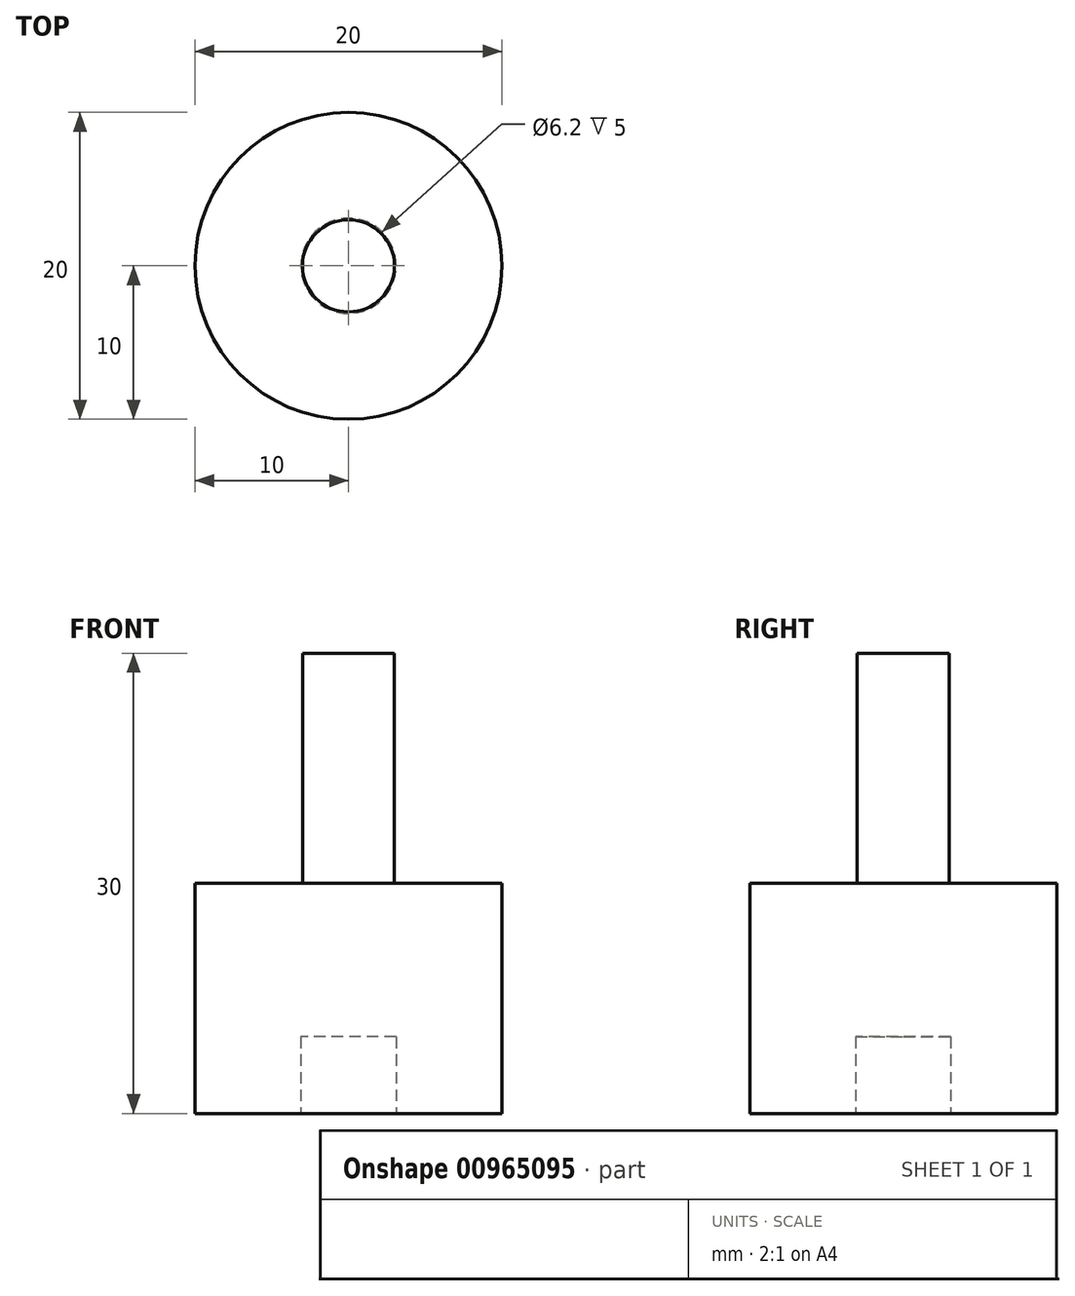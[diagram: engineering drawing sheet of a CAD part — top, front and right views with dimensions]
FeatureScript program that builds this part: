
annotation { "Feature Type Name" : "Feature", "Feature Type Description" : "" }
export const myFeature = defineFeature(function(context is Context, id is Id, definition is map)
    precondition{}
    {
        {
            var Q0;
            Q0=qCreatedBy(makeId("Top.planeOp"),FACE);
            var sketch = newSketch(context, id + "F0", { "sketchPlane" : qUnion([Q0])});
            skCircle(sketch, "E0", {"center": v(0, 0) * mm, "radius": 10 * mm});
            skCircle(sketch, "E1", {"center": v(0, 0) * mm, "radius": 3.1 * mm});
            skSolve(sketch);
        }
        {
            var Q0;
            Q0=makeQuery(id+"F0.imprint","IMPRINT",FACE,{"disambiguationData":[TD([[makeQuery(id+"F0.imprint","IMPRINT",EDGE,{"derivedFrom":sQuery(id+"F0.wireOp",EDGE,"E0")}),1.0]])]});
            extrude(context, id + "F1", {"entities" : qUnion([Q0]), "depth" : 5 * mm, "offsetDistance" : 25 * mm});
        }
        {
            var Q0;
            Q0=makeQuery(id+"F1.opExtrude","CAP_FACE",FACE,{"disambiguationData":[OSD([sQuery(id+"F0.wireOp",EDGE,"E0"),sQuery(id+"F0.wireOp",EDGE,"E1")])],"isStart":false});
            var sketch = newSketch(context, id + "F2", { "sketchPlane" : qUnion([Q0])});
            skCircle(sketch, "E2", {"center": v(0, 0) * mm, "radius": 3 * mm});
            skSolve(sketch);
        }
        {
            var Q0;
            Q0=makeQuery(id+"F2.imprint","IMPRINT",FACE,{"disambiguationData":[TD([[makeQuery(id+"F2.imprint","IMPRINT",EDGE,{"derivedFrom":makeQuery(id+"F1.opExtrude","CAP_EDGE",EDGE,{"disambiguationData":[OSD([sQuery(id+"F0.wireOp",EDGE,"E0")])],"isStart":false})}),1.0]])]});
            var Q1;
            Q1=makeQuery(id+"F2.imprint","IMPRINT",FACE,{"disambiguationData":[TD([[makeQuery(id+"F2.imprint","IMPRINT",EDGE,{"derivedFrom":sQuery(id+"F2.wireOp",EDGE,"E2")}),-1.0]])]});
            extrude(context, id + "F3", {"entities" : qUnion([Q0, Q1]), "operationType" : NewBodyOperationType.ADD, "depth" : 10 * mm, "offsetDistance" : 25 * mm});
        }
        {
            var Q0;
            Q0=makeQuery(id+"F2.imprint","IMPRINT",FACE,{"disambiguationData":[TD([[makeQuery(id+"F2.imprint","IMPRINT",EDGE,{"derivedFrom":sQuery(id+"F2.wireOp",EDGE,"E2")}),1.0]])]});
            extrude(context, id + "F4", {"entities" : qUnion([Q0]), "operationType" : NewBodyOperationType.ADD, "depth" : 25 * mm, "offsetDistance" : 25 * mm});
        }
    });
